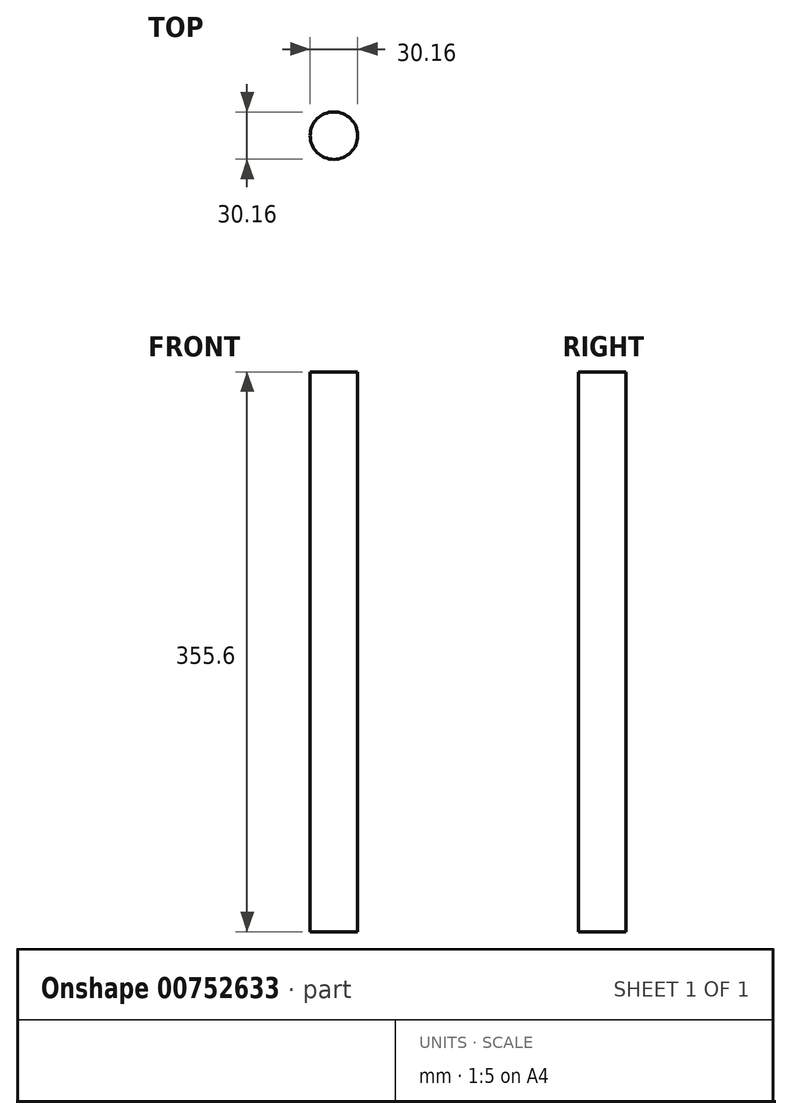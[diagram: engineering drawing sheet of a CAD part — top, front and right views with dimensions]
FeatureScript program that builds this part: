
annotation { "Feature Type Name" : "Feature", "Feature Type Description" : "" }
export const myFeature = defineFeature(function(context is Context, id is Id, definition is map)
    precondition{}
    {
        {
            var Q0;
            Q0=qCreatedBy(makeId("Top.planeOp"),FACE);
            cPlane(context, id + "F0", {"entities" : qUnion([Q0]), "cplaneType" : CPlaneType.OFFSET, "offset" : 31.75 * mm, "width" : 152.4 * mm, "height" : 152.4 * mm});
        }
        {
            var Q0;
            Q0=qCreatedBy(id+"F0.planeOp",FACE);
            var sketch = newSketch(context, id + "F1", { "sketchPlane" : qUnion([Q0])});
            skCircle(sketch, "E0", {"center": v(0, 0) * mm, "radius": 15.08 * mm});
            skSolve(sketch);
        }
        {
            var Q0;
            Q0 = qSketchRegion(id + "F1", true);
            extrude(context, id + "F2", {"entities" : qUnion([Q0]), "oppositeDirection" : true, "depth" : 355.6 * mm, "offsetDistance" : 25.4 * mm});
        }
    });
